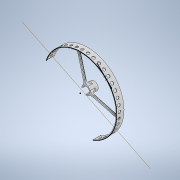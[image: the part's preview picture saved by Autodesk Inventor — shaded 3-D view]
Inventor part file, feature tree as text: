
AUTODESK INVENTOR PART (.ipt)
format: ipt  version: 2020 (Build 240168000, 168)  size: 1,056,256 bytes
history: native  units: in
note: dims shown in document units (in); Inventor stores cm internally (conversion verified against a paired STEP export)
features: sketch x7, extrude x6, fillet x4, other x3, plane x1, hole x1, pattern_linear x1
ambient origin geometry x8: Origin, YZ Plane, XZ Plane, XY Plane, X Axis, Y Axis, Z Axis, Center Point
bodies: Solid1 (feature_tree)
feature tree (23):
  extrude  "Extrusion1"  Depth=0.4224in
  extrude  "Extrusion2"  Depth=0.374in TaperAngle=0.0deg
  extrude  "Extrusion3"  Depth=1.063in
  fillet  "Fillet1"  Radius=0.0394in
  extrude  "Extrusion4"  Depth=3.4252in
  fillet  "Fillet5"  Radius=3.4882in
  fillet  "Fillet6"  Radius=0.2756in
  extrude  "Extrusion5"  Depth=0.7874in
  sketch  "Sketch7"  dims[d17=0.0787in d18=0.0in d19=0.2362in d23=0.7874in]
  plane  "Work Plane1"
  sketch  "3D Sketch1"
  other  "Work Point3"
  other  "Work Axis1"
  hole  "Hole1"  [1 undecoded]
  pattern_linear  "Rectangular Pattern1"  Spacing1=0.374in  [1 undecoded]
  extrude  "Extrusion6"  Depth=0.0276in
  fillet  "Fillet7"  Radius=0.1969in
  sketch  "Sketch1"  dims[d0=0.3228in d1=0.4224in]
  sketch  "Sketch2"  dims[d2=0.7696in d3=0.374in d4=0.0in]
  sketch  "Sketch3"  dims[d5=1.063in d6=1.063in d7=0.0394in d8=0.0in]
  sketch  "Sketch5"  dims[d9=1.5748in d11=360.0deg d13=3.4252in d14=3.4882in d15=0.2756in d16=0.0in]
  sketch  "Sketch8"  dims[d24=135.0deg d25=90.0deg d26=0.374in d27=0.0in d28=0.1575in d29=0.1969in d30=0.0276in d31=0.0276in d32=0.0276in d33=1.1811in d35=360.0deg d37=0.0394in d38=1.1811in d40=360.0deg d42=0.0394in d43=0.0in d44=-0.1378in d45=0.3937in d46=0.3937in d47=0.1378in d48=0.2362in d49=0.1575in d50=0.0787in d51=90.0deg d52=0.315in d53=0.8108in d54=7.874in d56=0.2756in d57=0.3543in d58=0.0in d59=0.0276in]
  other  "3D Intersection1"
note: 2 required parameter values undecoded (feature->parameter linkage not recoverable at this tier; creation-order binding heuristic only, values carry confidence <= 0.55)
